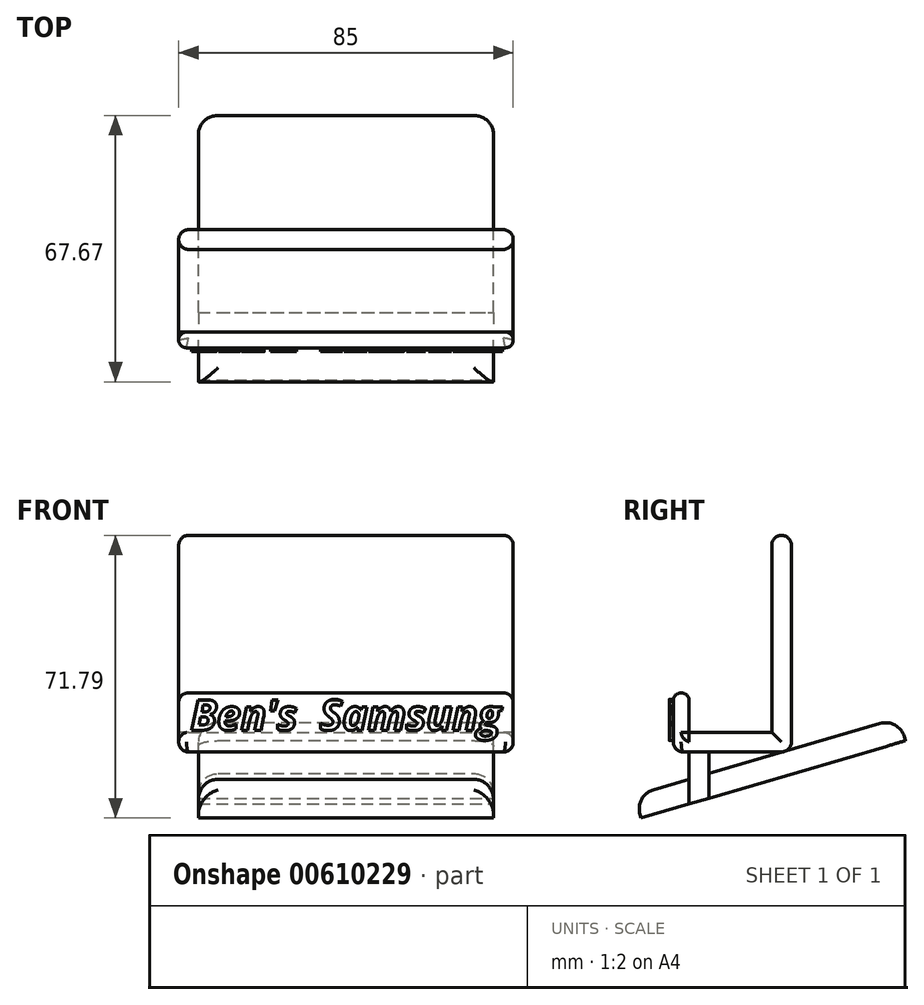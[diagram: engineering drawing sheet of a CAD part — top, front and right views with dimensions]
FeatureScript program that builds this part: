
annotation { "Feature Type Name" : "Feature", "Feature Type Description" : "" }
export const myFeature = defineFeature(function(context is Context, id is Id, definition is map)
    precondition{}
    {
        {
            var Q0;
            Q0=qCreatedBy(makeId("Front.planeOp"),FACE);
            var sketch = newSketch(context, id + "F0", { "sketchPlane" : qUnion([Q0])});
            skLineSegment(sketch, "E0.bottom", {"start": v(-1114.06, -547.87) * mm, "end": v(-1029.06, -547.87) * mm});
            skLineSegment(sketch, "E0.top", {"start": v(-1114.06, -597.87) * mm, "end": v(-1029.06, -597.87) * mm});
            skLineSegment(sketch, "E0.left", {"start": v(-1114.06, -547.87) * mm, "end": v(-1114.06, -597.87) * mm});
            skLineSegment(sketch, "E0.right", {"start": v(-1029.06, -547.87) * mm, "end": v(-1029.06, -597.87) * mm});
            skSolve(sketch);
        }
        {
            var Q0;
            Q0=makeQuery(id+"F0.imprint","IMPRINT",FACE,{"disambiguationData":[TD([[makeQuery(id+"F0.imprint","IMPRINT",EDGE,{"derivedFrom":sQuery(id+"F0.wireOp",EDGE,"E0.bottom")}),-1.0]])]});
            extrude(context, id + "F1", {"entities" : qUnion([Q0]), "depth" : 5 * mm, "offsetDistance" : 25 * mm});
        }
        {
            var Q0;
            Q0=makeQuery(id+"F1.opExtrude","CAP_FACE",FACE,{"disambiguationData":[OSD([sQuery(id+"F0.wireOp",EDGE,"E0.bottom"),sQuery(id+"F0.wireOp",EDGE,"E0.top"),sQuery(id+"F0.wireOp",EDGE,"E0.left"),sQuery(id+"F0.wireOp",EDGE,"E0.right")])],"isStart":false});
            var sketch = newSketch(context, id + "F2", { "sketchPlane" : qUnion([Q0])});
            skLineSegment(sketch, "E1.bottom", {"start": v(-1114.06, -597.87) * mm, "end": v(-1029.06, -597.87) * mm});
            skLineSegment(sketch, "E1.top", {"start": v(-1114.06, -602.87) * mm, "end": v(-1029.06, -602.87) * mm});
            skLineSegment(sketch, "E1.left", {"start": v(-1114.06, -602.87) * mm, "end": v(-1114.06, -597.87) * mm});
            skLineSegment(sketch, "E2", {"start": v(-1029.06, -597.87) * mm, "end": v(-1029.06, -602.87) * mm});
            skSolve(sketch);
        }
        {
            var Q0;
            Q0=makeQuery(id+"F2.imprint","IMPRINT",FACE,{"disambiguationData":[TD([[makeQuery(id+"F2.imprint","IMPRINT",EDGE,{"derivedFrom":sQuery(id+"F2.wireOp",EDGE,"E1.bottom")}),-1.0]])]});
            extrude(context, id + "F3", {"entities" : qUnion([Q0]), "operationType" : NewBodyOperationType.ADD, "depth" : 25 * mm, "offsetDistance" : 25 * mm, "hasSecondDirection" : true, "secondDirectionOppositeDirection" : true, "secondDirectionDepth" : 5 * mm});
        }
        {
            var Q0;
            Q0=makeQuery(id+"F3.opExtrude","SWEPT_FACE",FACE,{"disambiguationData":[OSD([sQuery(id+"F2.wireOp",EDGE,"E1.bottom")])]});
            var sketch = newSketch(context, id + "F4", { "sketchPlane" : qUnion([Q0])});
            skLineSegment(sketch, "E3.bottom", {"start": v(-1114.06, -30) * mm, "end": v(-1029.06, -30) * mm});
            skLineSegment(sketch, "E3.top", {"start": v(-1114.06, -26) * mm, "end": v(-1029.06, -26) * mm});
            skLineSegment(sketch, "E3.left", {"start": v(-1114.06, -30) * mm, "end": v(-1114.06, -26) * mm});
            skLineSegment(sketch, "E3.right", {"start": v(-1029.06, -30) * mm, "end": v(-1029.06, -26) * mm});
            skSolve(sketch);
        }
        {
            var Q0;
            Q0=makeQuery(id+"F4.imprint","IMPRINT",FACE,{"disambiguationData":[TD([[makeQuery(id+"F4.imprint","IMPRINT",EDGE,{"derivedFrom":sQuery(id+"F4.wireOp",EDGE,"E3.bottom")}),1.0]])]});
            extrude(context, id + "F5", {"entities" : qUnion([Q0]), "operationType" : NewBodyOperationType.ADD, "depth" : 10 * mm, "offsetDistance" : 25 * mm});
        }
        {
            var Q0;
            Q0=makeQuery(id+"F1.opExtrude","SWEPT_EDGE",EDGE,{"disambiguationData":[OSD([sQuery(id+"F0.wireOp",EDGE,"E0.bottom"),sQuery(id+"F0.wireOp",EDGE,"E0.right")])]});
            var Q1;
            Q1=makeQuery(id+"F5.opExtrude","CAP_EDGE",EDGE,{"disambiguationData":[OSD([sQuery(id+"F4.wireOp",EDGE,"E3.right")])],"isStart":false});
            var Q2;
            Q2=makeQuery(id+"F3.opExtrude","SWEPT_EDGE",EDGE,{"disambiguationData":[OSD([sQuery(id+"F2.wireOp",EDGE,"E1.top"),sQuery(id+"F2.wireOp",EDGE,"E2")])]});
            var Q3;
            Q3=makeQuery(id+"F3.boolean.opBoolean","MERGE",EDGE,{"derivedFrom":[makeQuery(id+"F1.opExtrude","CAP_EDGE",EDGE,{"disambiguationData":[OSD([sQuery(id+"F0.wireOp",EDGE,"E0.right")])],"isStart":true}),makeQuery(id+"F3.opExtrude","CAP_EDGE",EDGE,{"disambiguationData":[OSD([sQuery(id+"F2.wireOp",EDGE,"E2")])],"isStart":true})]});
            var Q4;
            Q4=makeQuery(id+"F1.opExtrude","CAP_EDGE",EDGE,{"disambiguationData":[OSD([sQuery(id+"F0.wireOp",EDGE,"E0.right")])],"isStart":false});
            var Q5;
            Q5=makeQuery(id+"F3.opExtrude","SWEPT_EDGE",EDGE,{"disambiguationData":[OSD([sQuery(id+"F0.wireOp",EDGE,"E0.right"),sQuery(id+"F2.wireOp",EDGE,"E1.bottom"),sQuery(id+"F2.wireOp",EDGE,"E2")])]});
            var Q6;
            Q6=makeQuery(id+"F1.opExtrude","CAP_EDGE",EDGE,{"disambiguationData":[OSD([sQuery(id+"F0.wireOp",EDGE,"E0.bottom")])],"isStart":false});
            var Q7;
            Q7=makeQuery(id+"F1.opExtrude","CAP_EDGE",EDGE,{"disambiguationData":[OSD([sQuery(id+"F0.wireOp",EDGE,"E0.bottom")])],"isStart":true});
            var Q8;
            Q8=makeQuery(id+"F1.opExtrude","SWEPT_EDGE",EDGE,{"disambiguationData":[OSD([sQuery(id+"F0.wireOp",EDGE,"E0.bottom"),sQuery(id+"F0.wireOp",EDGE,"E0.left")])]});
            var Q9;
            Q9=makeQuery(id+"F1.opExtrude","CAP_EDGE",EDGE,{"disambiguationData":[OSD([sQuery(id+"F0.wireOp",EDGE,"E0.left")])],"isStart":false});
            var Q10;
            Q10=makeQuery(id+"F3.boolean.opBoolean","MERGE",EDGE,{"derivedFrom":[makeQuery(id+"F1.opExtrude","CAP_EDGE",EDGE,{"disambiguationData":[OSD([sQuery(id+"F0.wireOp",EDGE,"E0.left")])],"isStart":true}),makeQuery(id+"F3.opExtrude","CAP_EDGE",EDGE,{"disambiguationData":[OSD([sQuery(id+"F2.wireOp",EDGE,"E1.left")])],"isStart":true})]});
            var Q11;
            Q11=makeQuery(id+"F3.opExtrude","SWEPT_EDGE",EDGE,{"disambiguationData":[OSD([sQuery(id+"F2.wireOp",EDGE,"E1.top"),sQuery(id+"F2.wireOp",EDGE,"E1.left")])]});
            var Q12;
            Q12=makeQuery(id+"F3.opExtrude","CAP_EDGE",EDGE,{"disambiguationData":[OSD([sQuery(id+"F2.wireOp",EDGE,"E1.top")])],"isStart":true});
            var Q13;
            Q13=makeQuery(id+"F3.opExtrude","CAP_EDGE",EDGE,{"disambiguationData":[OSD([sQuery(id+"F2.wireOp",EDGE,"E1.top")])],"isStart":false});
            var Q14;
            Q14=makeQuery(id+"F3.opExtrude","SWEPT_EDGE",EDGE,{"disambiguationData":[OSD([sQuery(id+"F0.wireOp",EDGE,"E0.left"),sQuery(id+"F2.wireOp",EDGE,"E1.bottom"),sQuery(id+"F2.wireOp",EDGE,"E1.left")])]});
            var Q15;
            Q15=makeQuery(id+"F5.opExtrude","CAP_EDGE",EDGE,{"disambiguationData":[OSD([sQuery(id+"F4.wireOp",EDGE,"E3.left")])],"isStart":false});
            fillet(context, id + "F6", {"entities" : qUnion([Q0, Q1, Q2, Q3, Q4, Q5, Q6, Q7, Q8, Q9, Q10, Q11, Q12, Q13, Q14, Q15]), "radius" : 2.5 * mm, "tangentPropagation" : true, "allowEdgeOverflow" : false});
        }
        {
            var Q0;
            Q0=makeQuery(id+"F5.boolean.opBoolean","MERGE",EDGE,{"derivedFrom":[makeQuery(id+"F3.opExtrude","CAP_EDGE",EDGE,{"disambiguationData":[OSD([sQuery(id+"F2.wireOp",EDGE,"E1.left")])],"isStart":false}),makeQuery(id+"F5.opExtrude","SWEPT_EDGE",EDGE,{"disambiguationData":[OSD([sQuery(id+"F4.wireOp",EDGE,"E3.bottom"),sQuery(id+"F4.wireOp",EDGE,"E3.left")])]})]});
            var Q1;
            Q1=makeQuery(id+"F6.opFillet","BLEND_EDGE",EDGE,{"blendedFrom":[makeQuery(id+"F5.opExtrude","CAP_EDGE",EDGE,{"disambiguationData":[OSD([sQuery(id+"F4.wireOp",EDGE,"E3.left")])],"isStart":false}),makeQuery(id+"F5.opExtrude","SWEPT_FACE",FACE,{"disambiguationData":[OSD([sQuery(id+"F4.wireOp",EDGE,"E3.top")])]})],"blendedInto":[makeQuery(id+"F5.opExtrude","SWEPT_FACE",FACE,{"disambiguationData":[OSD([sQuery(id+"F4.wireOp",EDGE,"E3.top")])]})]});
            fillet(context, id + "F7", {"entities" : qUnion([Q0, Q1]), "radius" : 2 * mm, "tangentPropagation" : true, "allowEdgeOverflow" : false});
        }
        {
            var Q0;
            Q0=makeQuery(id+"F3.opExtrude","SWEPT_FACE",FACE,{"disambiguationData":[OSD([sQuery(id+"F2.wireOp",EDGE,"E1.top")])]});
            var sketch = newSketch(context, id + "F8", { "sketchPlane" : qUnion([Q0])});
            skLineSegment(sketch, "E4.bottom", {"start": v(-1109.06, 21) * mm, "end": v(-1034.06, 21) * mm});
            skLineSegment(sketch, "E4.top", {"start": v(-1109.06, 26) * mm, "end": v(-1034.06, 26) * mm});
            skLineSegment(sketch, "E4.left", {"start": v(-1109.06, 21) * mm, "end": v(-1109.06, 26) * mm});
            skLineSegment(sketch, "E4.right", {"start": v(-1034.06, 21) * mm, "end": v(-1034.06, 26) * mm});
            skSolve(sketch);
        }
        {
            var Q0;
            Q0=makeQuery(id+"F8.imprint","IMPRINT",FACE,{"disambiguationData":[TD([[makeQuery(id+"F8.imprint","IMPRINT",EDGE,{"derivedFrom":sQuery(id+"F8.wireOp",EDGE,"E4.bottom")}),1.0]])]});
            extrude(context, id + "F9", {"entities" : qUnion([Q0]), "operationType" : NewBodyOperationType.ADD, "depth" : 25 * mm, "offsetDistance" : 25 * mm});
        }
        {
            var Q0;
            Q0=makeQuery(id+"F9.opExtrude","SWEPT_FACE",FACE,{"disambiguationData":[OSD([sQuery(id+"F8.wireOp",EDGE,"E4.right")])]});
            var sketch = newSketch(context, id + "F10", { "sketchPlane" : qUnion([Q0])});
            skLineSegment(sketch, "E5", {"start": v(-39.87, -613.9) * mm, "end": v(27.32, -594.26) * mm});
            skLineSegment(sketch, "E6", {"start": v(-39.87, -613.9) * mm, "end": v(-38.19, -619.66) * mm});
            skLineSegment(sketch, "E7", {"start": v(-38.19, -619.66) * mm, "end": v(29, -600.02) * mm});
            skLineSegment(sketch, "E8", {"start": v(29, -600.02) * mm, "end": v(27.32, -594.26) * mm});
            skSolve(sketch);
        }
        {
            var Q0;
            {var subQ0=sQuery(id+"F10.wireOp",EDGE,"E8");Q0=makeQuery(id+"F10.imprint","IMPRINT",FACE,{"disambiguationData":[TD([[makeQuery(id+"F10.imprint","IMPRINT",EDGE,{"derivedFrom":subQ0}),1.0]])]});}
            var Q1;
            {var subQ0=sQuery(id+"F10.wireOp",EDGE,"E6");Q1=makeQuery(id+"F10.imprint","IMPRINT",FACE,{"disambiguationData":[TD([[makeQuery(id+"F10.imprint","IMPRINT",EDGE,{"derivedFrom":subQ0}),1.0]])]});}
            extrude(context, id + "F11", {"entities" : qUnion([Q0, Q1]), "oppositeDirection" : true, "depth" : 75 * mm, "offsetDistance" : 25 * mm});
        }
        {
            var Q0;
            Q0=makeQuery(id+"F9.opExtrude","SWEPT_FACE",FACE,{"disambiguationData":[OSD([sQuery(id+"F8.wireOp",EDGE,"E4.left")])]});
            var sketch = newSketch(context, id + "F12", { "sketchPlane" : qUnion([Q0])});
            skLineSegment(sketch, "E9", {"start": v(21, -614.64) * mm, "end": v(26, -616.1) * mm});
            skSolve(sketch);
        }
        {
            var Q0;
            {var subQ0=sQuery(id+"F12.wireOp",EDGE,"E9");Q0=makeQuery(id+"F12.imprint","IMPRINT",FACE,{"disambiguationData":[TD([[makeQuery(id+"F12.imprint","IMPRINT",EDGE,{"derivedFrom":subQ0}),-1.0]])]});}
            extrude(context, id + "F13", {"entities" : qUnion([Q0]), "operationType" : NewBodyOperationType.REMOVE, "oppositeDirection" : true, "depth" : 80 * mm, "offsetDistance" : 25 * mm});
        }
        {
            var Q0;
            Q0=makeQuery(id+"F11.opExtrude","CAP_EDGE",EDGE,{"disambiguationData":[OSD([sQuery(id+"F10.wireOp",EDGE,"E8")])],"isStart":true});
            var Q1;
            {var subQ0=sQuery(id+"F10.wireOp",EDGE,"E5");Q1=makeQuery(id+"F11.opExtrude","CAP_EDGE",EDGE,{"disambiguationData":[OSD([subQ0]),TDD([makeQuery(id+"F10.imprint","IMPRINT",EDGE,{"disambiguationData":[TD([[makeQuery(id+"F10.imprint","INTERSECT",VERTEX,{"derivedFrom":[subQ0,sQuery(id+"F10.wireOp",EDGE,"E8")]}),1.0]])],"derivedFrom":subQ0})])],"isStart":true});}
            var Q2;
            Q2=makeQuery(id+"F11.opExtrude","SWEPT_EDGE",EDGE,{"disambiguationData":[OSD([sQuery(id+"F10.wireOp",EDGE,"E5"),sQuery(id+"F10.wireOp",EDGE,"E8")])]});
            var Q3;
            Q3=makeQuery(id+"F11.opExtrude","CAP_EDGE",EDGE,{"disambiguationData":[OSD([sQuery(id+"F10.wireOp",EDGE,"E8")])],"isStart":false});
            var Q4;
            {var subQ0=sQuery(id+"F10.wireOp",EDGE,"E5");Q4=makeQuery(id+"F11.opExtrude","CAP_EDGE",EDGE,{"disambiguationData":[OSD([subQ0]),TDD([makeQuery(id+"F10.imprint","IMPRINT",EDGE,{"disambiguationData":[TD([[makeQuery(id+"F10.imprint","INTERSECT",VERTEX,{"derivedFrom":[subQ0,sQuery(id+"F10.wireOp",EDGE,"E8")]}),1.0]])],"derivedFrom":subQ0})])],"isStart":false});}
            var Q5;
            {var subQ0=sQuery(id+"F10.wireOp",EDGE,"E5");Q5=makeQuery(id+"F11.opExtrude","CAP_EDGE",EDGE,{"disambiguationData":[OSD([subQ0]),TDD([makeQuery(id+"F10.imprint","IMPRINT",EDGE,{"disambiguationData":[TD([[makeQuery(id+"F10.imprint","INTERSECT",VERTEX,{"derivedFrom":[subQ0,sQuery(id+"F10.wireOp",EDGE,"E6")]}),-1.0]])],"derivedFrom":subQ0})])],"isStart":false});}
            var Q6;
            Q6=makeQuery(id+"F11.opExtrude","SWEPT_EDGE",EDGE,{"disambiguationData":[OSD([sQuery(id+"F10.wireOp",EDGE,"E5"),sQuery(id+"F10.wireOp",EDGE,"E6")])]});
            var Q7;
            {var subQ0=sQuery(id+"F10.wireOp",EDGE,"E5");Q7=makeQuery(id+"F11.opExtrude","CAP_EDGE",EDGE,{"disambiguationData":[OSD([subQ0]),TDD([makeQuery(id+"F10.imprint","IMPRINT",EDGE,{"disambiguationData":[TD([[makeQuery(id+"F10.imprint","INTERSECT",VERTEX,{"derivedFrom":[subQ0,sQuery(id+"F10.wireOp",EDGE,"E6")]}),-1.0]])],"derivedFrom":subQ0})])],"isStart":true});}
            fillet(context, id + "F14", {"entities" : qUnion([Q0, Q1, Q2, Q3, Q4, Q5, Q6, Q7]), "radius" : 5 * mm, "tangentPropagation" : true, "allowEdgeOverflow" : false});
        }
        {
            var Q0;
            Q0=makeQuery(id+"F5.boolean.opBoolean","MERGE",FACE,{"derivedFrom":[makeQuery(id+"F3.opExtrude","CAP_FACE",FACE,{"disambiguationData":[OSD([sQuery(id+"F2.wireOp",EDGE,"E1.bottom"),sQuery(id+"F2.wireOp",EDGE,"E1.top"),sQuery(id+"F2.wireOp",EDGE,"E1.left"),sQuery(id+"F2.wireOp",EDGE,"E2")])],"isStart":false}),makeQuery(id+"F5.opExtrude","SWEPT_FACE",FACE,{"disambiguationData":[OSD([sQuery(id+"F4.wireOp",EDGE,"E3.bottom")])]})]});
            var sketch = newSketch(context, id + "F15", { "sketchPlane" : qUnion([Q0])});
            skText(sketch, "E10", { "text": "Ben\'s  Samsung", "fontName": "OpenSans-BoldItalic.ttf"});
            const initialGuessF15  = {"E10": [-1.11106, -0.59737, 1, 0, 0.0078]};
            skSetInitialGuess(sketch, initialGuessF15);
            skSolve(sketch);
        }
        {
            var Q0;
            Q0 = qSketchRegion(id + "F15", true);
            extrude(context, id + "F16", {"entities" : qUnion([Q0]), "operationType" : NewBodyOperationType.ADD, "depth" : 1 * mm, "offsetDistance" : 25 * mm});
        }
    });
